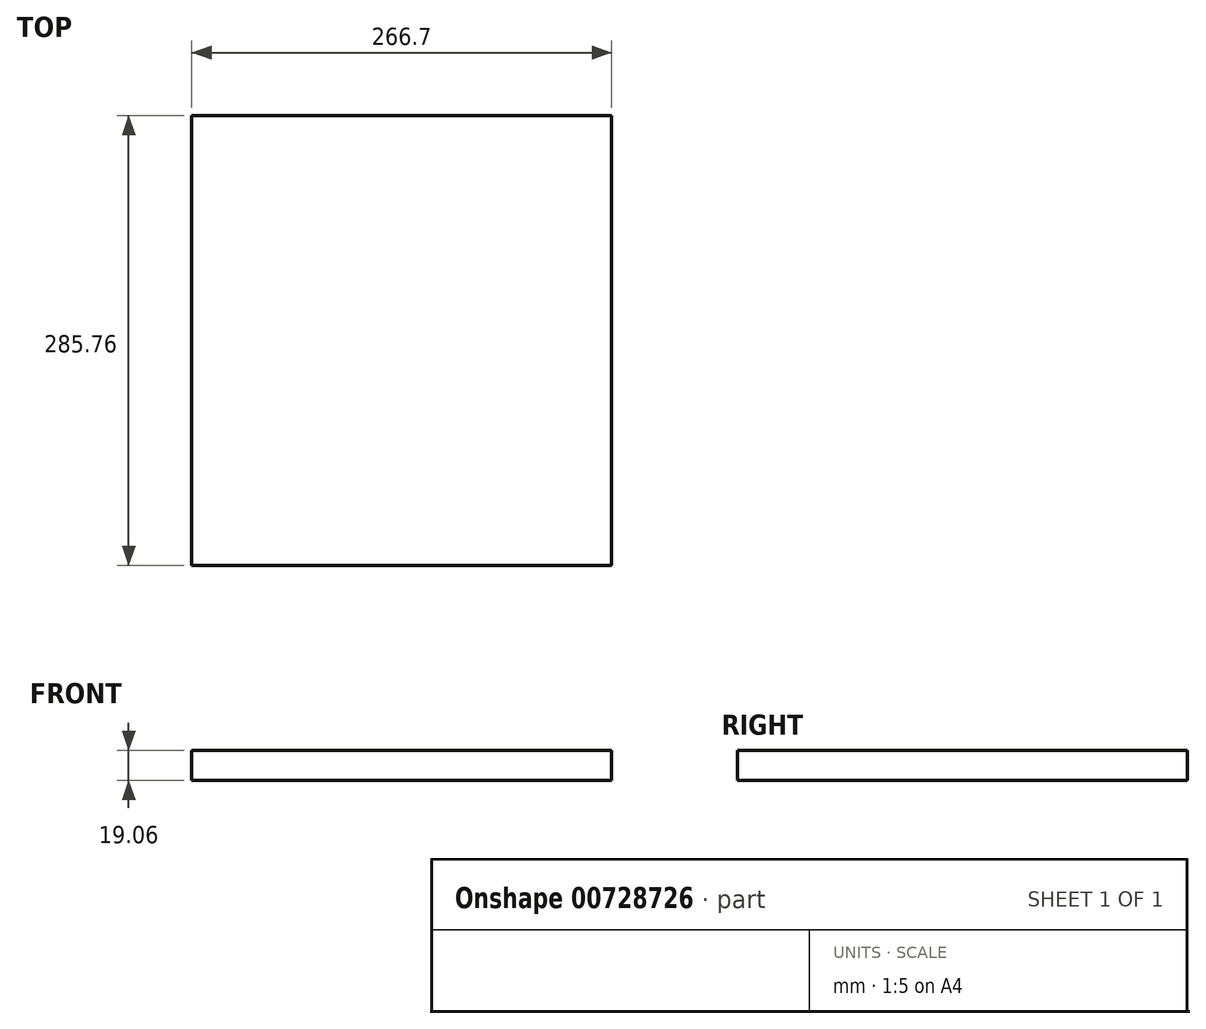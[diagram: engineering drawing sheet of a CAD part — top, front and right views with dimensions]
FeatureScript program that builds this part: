
annotation { "Feature Type Name" : "Feature", "Feature Type Description" : "" }
export const myFeature = defineFeature(function(context is Context, id is Id, definition is map)
    precondition{}
    {
        {
            var Q0;
            Q0=qCreatedBy(makeId("Right.planeOp"),FACE);
            var sketch = newSketch(context, id + "F0", { "sketchPlane" : qUnion([Q0])});
            skLineSegment(sketch, "E0.bottom", {"start": v(142.87, 9.53) * mm, "end": v(-142.88, 9.53) * mm});
            skLineSegment(sketch, "E0.top", {"start": v(142.87, -9.53) * mm, "end": v(-142.88, -9.53) * mm});
            skLineSegment(sketch, "E0.left", {"start": v(142.87, 9.53) * mm, "end": v(142.87, -9.53) * mm});
            skLineSegment(sketch, "E0.right", {"start": v(-142.88, 9.53) * mm, "end": v(-142.88, -9.53) * mm});
            skPoint(sketch, "E0.middle", {"position": v(0, 0) * mm});
            skSolve(sketch);
        }
        {
            var Q0;
            Q0 = qSketchRegion(id + "F0", true);
            extrude(context, id + "F1", {"entities" : qUnion([Q0]), "depth" : 266.7 * mm, "offsetDistance" : 25.4 * mm});
        }
    });
